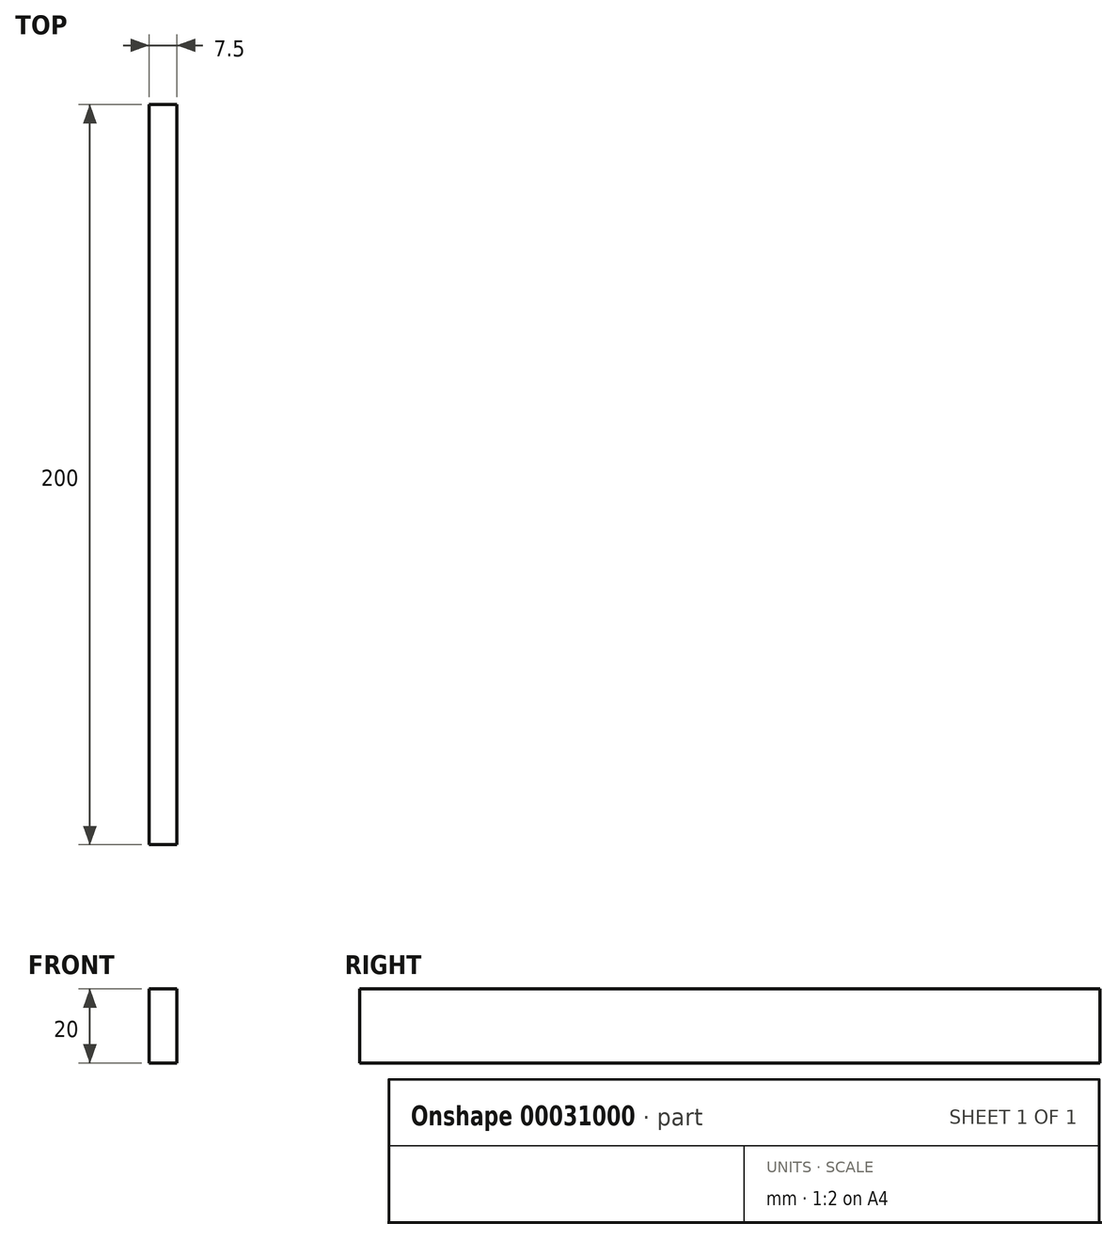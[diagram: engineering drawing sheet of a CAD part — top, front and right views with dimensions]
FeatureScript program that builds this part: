
annotation { "Feature Type Name" : "Feature", "Feature Type Description" : "" }
export const myFeature = defineFeature(function(context is Context, id is Id, definition is map)
    precondition{}
    {
        {
            var Q0;
            Q0=qCreatedBy(makeId("Front.planeOp"),FACE);
            var sketch = newSketch(context, id + "F0", { "sketchPlane" : qUnion([Q0])});
            skLineSegment(sketch, "E0.rect.bottom", {"start": v(3.75, 10) * mm, "end": v(-3.75, 10) * mm});
            skLineSegment(sketch, "E0.rect.top", {"start": v(3.75, -10) * mm, "end": v(-3.75, -10) * mm});
            skLineSegment(sketch, "E0.rect.left", {"start": v(3.75, 10) * mm, "end": v(3.75, -10) * mm});
            skLineSegment(sketch, "E0.rect.right", {"start": v(-3.75, 10) * mm, "end": v(-3.75, -10) * mm});
            skPoint(sketch, "E0.rect.middle", {"position": v(0, 0) * mm});
            skSolve(sketch);
        }
        {
            var Q0;
            Q0 = qSketchRegion(id + "F0", true);
            extrude(context, id + "F1", {"entities" : qUnion([Q0]), "depth" : 200 * mm});
        }
    });
